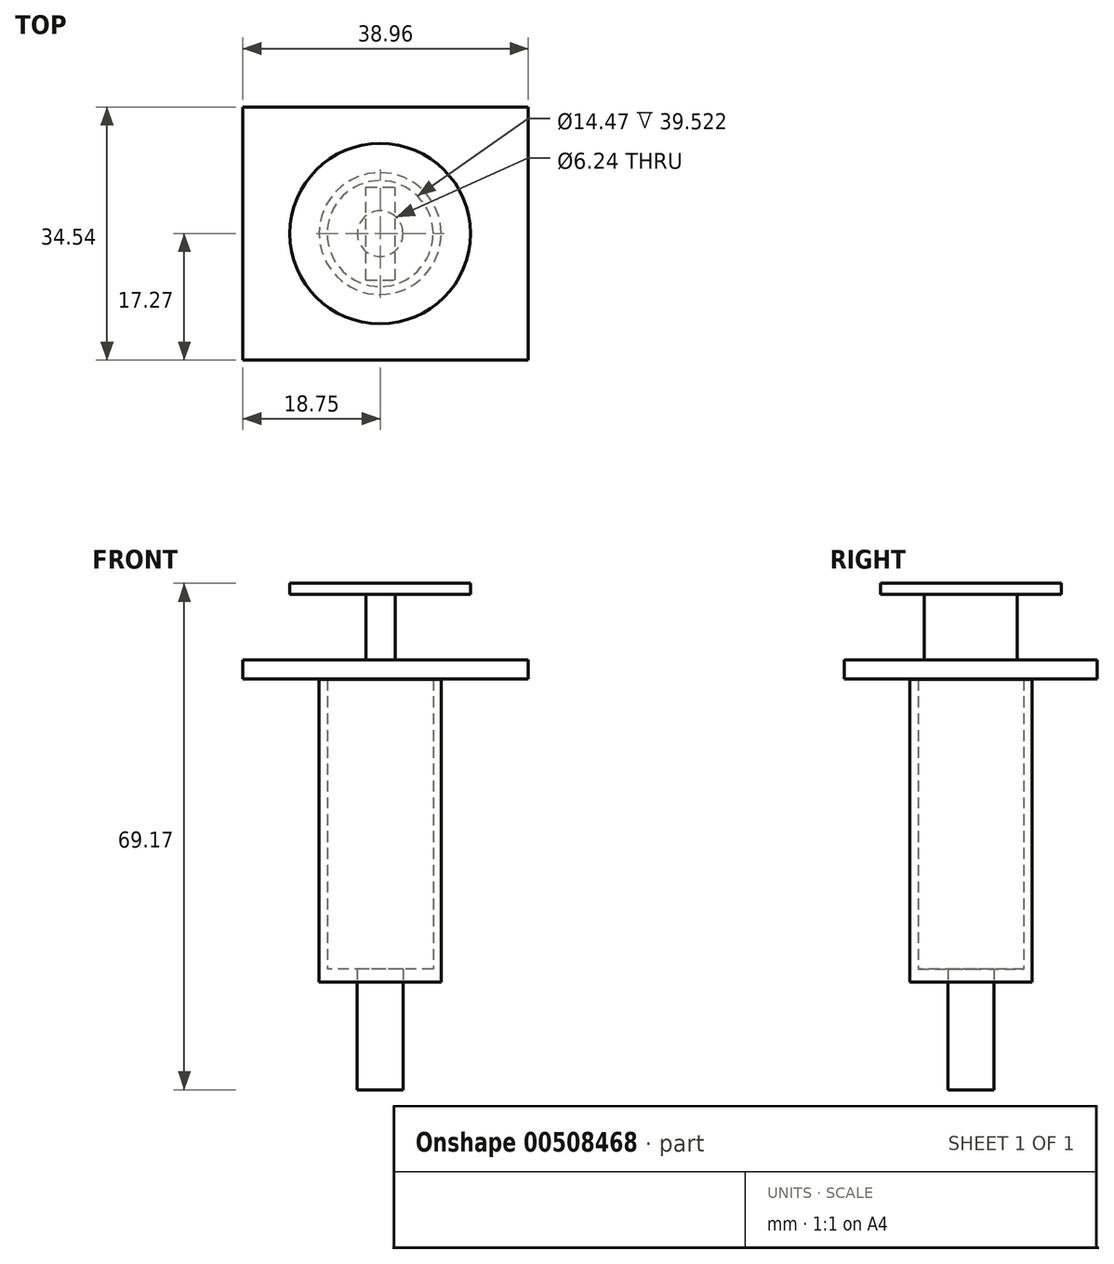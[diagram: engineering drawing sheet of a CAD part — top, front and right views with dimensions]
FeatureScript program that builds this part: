
annotation { "Feature Type Name" : "Feature", "Feature Type Description" : "" }
export const myFeature = defineFeature(function(context is Context, id is Id, definition is map)
    precondition{}
    {
        {
            var Q0;
            Q0=qCreatedBy(makeId("Top.planeOp"),FACE);
            var sketch = newSketch(context, id + "F0", { "sketchPlane" : qUnion([Q0])});
            skCircle(sketch, "E0", {"center": v(0, 0) * mm, "radius": 8.33 * mm});
            skCircle(sketch, "E1", {"center": v(0, 0) * mm, "radius": 7.23 * mm});
            skCircle(sketch, "E2", {"center": v(0, 0) * mm, "radius": 3.12 * mm});
            skSolve(sketch);
        }
        {
            var Q0;
            Q0 = qSketchRegion(id + "F0", true);
            extrude(context, id + "F1", {"entities" : qUnion([Q0]), "depth" : 41.3 * mm});
        }
        {
            var Q0;
            Q0=sQuery(id+"F0.wireOp",EDGE,"E1");
            extrude(context, id + "F2", {"bodyType" : ToolBodyType.SURFACE, "surfaceEntities" : qUnion([Q0]), "depth" : 25.4 * mm});
        }
        {
            var Q0;
            Q0=makeQuery(id+"F0.imprint","IMPRINT",FACE,{"disambiguationData":[TD([[makeQuery(id+"F0.imprint","IMPRINT",EDGE,{"derivedFrom":sQuery(id+"F0.wireOp",EDGE,"E1")}),1.0]])]});
            extrude(context, id + "F3", {"entities" : qUnion([Q0]), "operationType" : NewBodyOperationType.ADD, "depth" : 1.78 * mm});
        }
        {
            var Q0;
            Q0=makeQuery(id+"F0.imprint","IMPRINT",FACE,{"disambiguationData":[TD([[makeQuery(id+"F0.imprint","IMPRINT",EDGE,{"derivedFrom":sQuery(id+"F0.wireOp",EDGE,"E2")}),1.0]])]});
            extrude(context, id + "F4", {"entities" : qUnion([Q0]), "oppositeDirection" : true, "depth" : 14.73 * mm});
        }
        {
            var Q0;
            Q0=qCreatedBy(makeId("Front.planeOp"),FACE);
            var sketch = newSketch(context, id + "F5", { "sketchPlane" : qUnion([Q0])});
            skLineSegment(sketch, "E3", {"start": v(0, 41.36) * mm, "end": v(-18.75, 41.36) * mm});
            skLineSegment(sketch, "E4", {"start": v(0, 41.36) * mm, "end": v(20.21, 41.36) * mm});
            skLineSegment(sketch, "E5", {"start": v(-18.75, 41.36) * mm, "end": v(-18.75, 43.97) * mm});
            skLineSegment(sketch, "E6", {"start": v(-18.75, 43.97) * mm, "end": v(20.21, 43.97) * mm});
            skLineSegment(sketch, "E7", {"start": v(20.21, 41.36) * mm, "end": v(20.21, 43.97) * mm});
            skSolve(sketch);
        }
        {
            var Q0;
            Q0 = qSketchRegion(id + "F5", true);
            extrude(context, id + "F6", {"entities" : qUnion([Q0]), "endBound" : BoundingType.SYMMETRIC, "oppositeDirection" : true, "depth" : 34.54 * mm});
        }
        {
            var Q0;
            Q0=qCreatedBy(makeId("Front.planeOp"),FACE);
            var sketch = newSketch(context, id + "F7", { "sketchPlane" : qUnion([Q0])});
            skLineSegment(sketch, "E8", {"start": v(-1.94, 43.96) * mm, "end": v(-1.94, 52.96) * mm});
            skLineSegment(sketch, "E9", {"start": v(2.04, 43.96) * mm, "end": v(2.04, 52.96) * mm});
            skLineSegment(sketch, "E10", {"start": v(-1.94, 52.96) * mm, "end": v(2.04, 52.96) * mm});
            skLineSegment(sketch, "E11", {"start": v(-1.94, 43.96) * mm, "end": v(2.04, 43.96) * mm});
            skSolve(sketch);
        }
        {
            var Q0;
            Q0=makeQuery(id+"F7.imprint","IMPRINT",FACE,{"disambiguationData":[TD([[makeQuery(id+"F7.imprint","IMPRINT",EDGE,{"derivedFrom":sQuery(id+"F7.wireOp",EDGE,"E8")}),-1.0]])]});
            extrude(context, id + "F8", {"entities" : qUnion([Q0]), "endBound" : BoundingType.SYMMETRIC, "depth" : 12.7 * mm});
        }
        {
            var Q0;
            Q0=qCreatedBy(makeId("Right.planeOp"),FACE);
            var sketch = newSketch(context, id + "F9", { "sketchPlane" : qUnion([Q0])});
            skLineSegment(sketch, "E12", {"start": v(-1.86, 52.8) * mm, "end": v(-1.86, 44.05) * mm});
            skLineSegment(sketch, "E13", {"start": v(1.82, 52.8) * mm, "end": v(1.82, 44) * mm});
            skLineSegment(sketch, "E14", {"start": v(-1.86, 52.8) * mm, "end": v(1.82, 52.8) * mm});
            skLineSegment(sketch, "E15", {"start": v(-1.86, 44.05) * mm, "end": v(1.82, 44) * mm});
            skSolve(sketch);
        }
        {
            var Q0;
            Q0=sQuery(id+"F9.wireOp",EDGE,"E15");
            var Q1;
            Q1=sQuery(id+"F9.wireOp",EDGE,"E12");
            var Q2;
            Q2=sQuery(id+"F9.wireOp",EDGE,"E13");
            var Q3;
            Q3=sQuery(id+"F9.wireOp",EDGE,"E14");
            extrude(context, id + "F10", {"bodyType" : ToolBodyType.SURFACE, "surfaceEntities" : qUnion([Q0, Q1, Q2, Q3]), "endBound" : BoundingType.SYMMETRIC, "depth" : 12.7 * mm});
        }
        {
            var Q0;
            Q0=makeQuery(id+"F8.opExtrude","SWEPT_FACE",FACE,{"disambiguationData":[OSD([sQuery(id+"F7.wireOp",EDGE,"E10")])]});
            var sketch = newSketch(context, id + "F11", { "sketchPlane" : qUnion([Q0])});
            skCircle(sketch, "E16", {"center": v(0, 0) * mm, "radius": 12.33 * mm});
            skSolve(sketch);
        }
        {
            var Q0;
            Q0 = qSketchRegion(id + "F11", true);
            var Q1;
            Q1=makeQuery(id+"F11.imprint","IMPRINT",FACE,{"disambiguationData":[TD([[makeQuery(id+"F11.imprint","IMPRINT",EDGE,{"derivedFrom":sQuery(id+"F11.wireOp",EDGE,"E16")}),1.0]])]});
            extrude(context, id + "F12", {"entities" : qUnion([Q0, Q1]), "operationType" : NewBodyOperationType.ADD, "depth" : 1.47 * mm});
        }
    });
